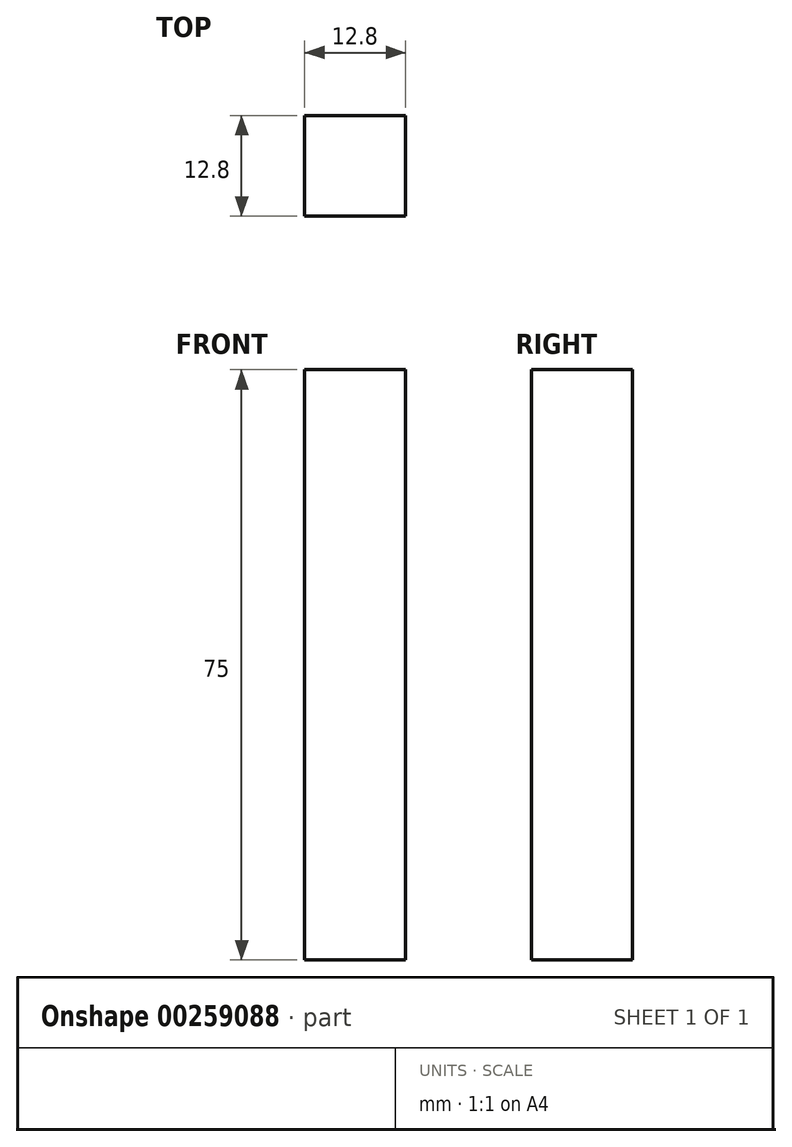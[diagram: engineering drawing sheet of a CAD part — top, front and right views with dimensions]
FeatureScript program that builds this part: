
annotation { "Feature Type Name" : "Feature", "Feature Type Description" : "" }
export const myFeature = defineFeature(function(context is Context, id is Id, definition is map)
    precondition{}
    {
        {
            var Q0;
            Q0=qCreatedBy(makeId("Top.planeOp"),FACE);
            var sketch = newSketch(context, id + "F0", { "sketchPlane" : qUnion([Q0])});
            skLineSegment(sketch, "E0.bottom", {"start": v(6.4, -6.4) * mm, "end": v(-6.4, -6.4) * mm});
            skLineSegment(sketch, "E0.top", {"start": v(6.4, 6.4) * mm, "end": v(-6.4, 6.4) * mm});
            skLineSegment(sketch, "E0.left", {"start": v(6.4, -6.4) * mm, "end": v(6.4, 6.4) * mm});
            skLineSegment(sketch, "E0.right", {"start": v(-6.4, -6.4) * mm, "end": v(-6.4, 6.4) * mm});
            skPoint(sketch, "E0.middle", {"position": v(0, 0) * mm});
            skSolve(sketch);
        }
        {
            var Q0;
            Q0=qSketchRegion(id+"F0",true);
            extrude(context, id + "F1", {"entities" : qUnion([Q0]), "depth" : 75 * mm});
        }
    });
